# Revit family: Accessory-Shower_Basket-KOHLER-Medium-K-1896
name_source: partatom
category: Specialty Equipment
revit_build: Autodesk Revit 2015 (Build: 20140606_1530(x64)
units: mm (PartAtom-declared; Revit-internal decimal feet)

## types (6) — shared parameters
ADA Compliant = No
Assembly Code = C1030200
Date Modified = 08/29/2018
Default Elevation = 42"
Description = Medium shower basket
Height = 3"
Length = 9 1/4"
Manufacturer = KOHLER Co.
MasterFormat 1995 = 10820
MasterFormat 2004 = 10.28.13
Material = Stainless-Steel Construction
Product Documentation Link = http://www.us.kohler.com
Product Name = Medium
Product Page URL = http://www.us.kohler.com
URL = https://www.us.kohler.com
Width = 6 1/4"

## per-type parameters (varying)
| type | Finish | Model | Type |
| S - Polished Stainless | Kohler-Metal-S-Polished_Stainless | K-1896-S | 1 |
| SN - Vibrant Polished Nickel | Kohler-Metal-SN-Vibrant_Polished_Nickel | K-1896-SN | 2 |
| AF - Vibrant French Gold | Kohler-Metal-AF-Vibrant_French_Gold | K-1896-AF | 3 |
| BS - Brushed Stainless | Kohler-Metal-BS-Brushed_Stainless | K-1896-BS | 4 |
| BV - Vibrant Brushed Bronze | Kohler-Metal-BV-Brushed_Bronze | K-1896-BV | 5 |
| 2BZ - Oil-Rubbed Bronze | Kohler-Metal-2BZ-Oil_Rubbed_Bronze | K-1896-2BZ | 6 |

## geometry (parser evidence)
native form markers: Sweep x2
no freeform markers — native parametric forms only
